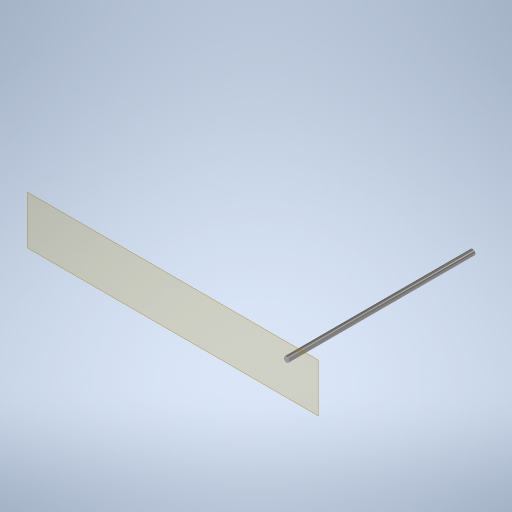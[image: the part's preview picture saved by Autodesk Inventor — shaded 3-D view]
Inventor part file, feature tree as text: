
AUTODESK INVENTOR PART (.ipt)
format: ipt  version: 2023 (Build 270158030, 158C)  size: 243,712 bytes
history: native  units: mm
features: other x2, plane x1, extrude x1, sketch x1, reference x1
ambient origin geometry x8: Origin, YZ Plane, XZ Plane, XY Plane, X Axis, Y Axis, Z Axis, Center Point
bodies: Solid1 (feature_tree)
feature tree (6):
  plane  "Work Plane1"
  extrude  "Extrusion1"  Depth=3.0mm TaperAngle=0.0deg
  sketch  "Sketch1"  dims[d0=1.6mm d1=3.0mm d2=53.0mm d3=0.0mm d4=0.0mm]
  reference  "Reference1"
  other  "Assembly1"
  other  "s20-phone-clip:1"
